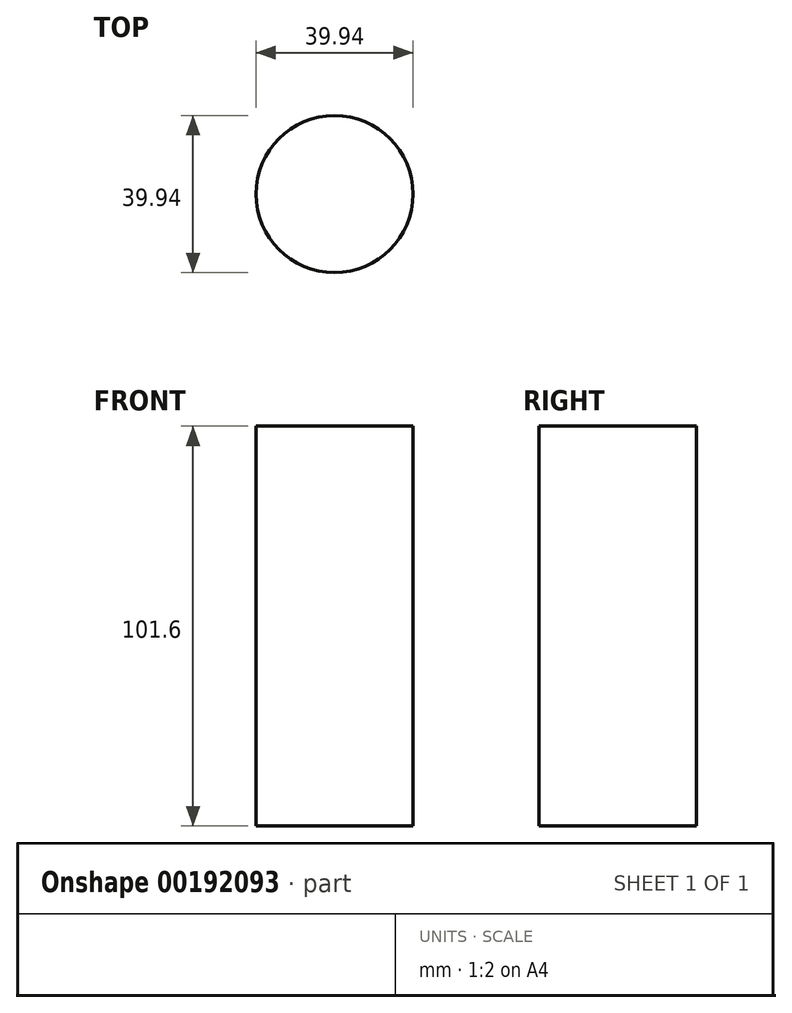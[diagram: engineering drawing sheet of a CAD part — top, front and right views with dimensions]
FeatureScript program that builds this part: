
annotation { "Feature Type Name" : "Feature", "Feature Type Description" : "" }
export const myFeature = defineFeature(function(context is Context, id is Id, definition is map)
    precondition{}
    {
        {
            var Q0;
            Q0=qCreatedBy(makeId("Top.planeOp"),FACE);
            var sketch = newSketch(context, id + "F0", { "sketchPlane" : qUnion([Q0])});
            skCircle(sketch, "E0", {"center": v(0, 0) * mm, "radius": 19.97 * mm});
            skSolve(sketch);
        }
        {
            var Q0;
            Q0=makeQuery(id+"F0.imprint","IMPRINT",FACE,{"disambiguationData":[TD([[makeQuery(id+"F0.imprint","IMPRINT",EDGE,{"derivedFrom":sQuery(id+"F0.wireOp",EDGE,"E0")}),1.0]])]});
            extrude(context, id + "F1", {"entities" : qUnion([Q0]), "depth" : 101.6 * mm});
        }
    });
